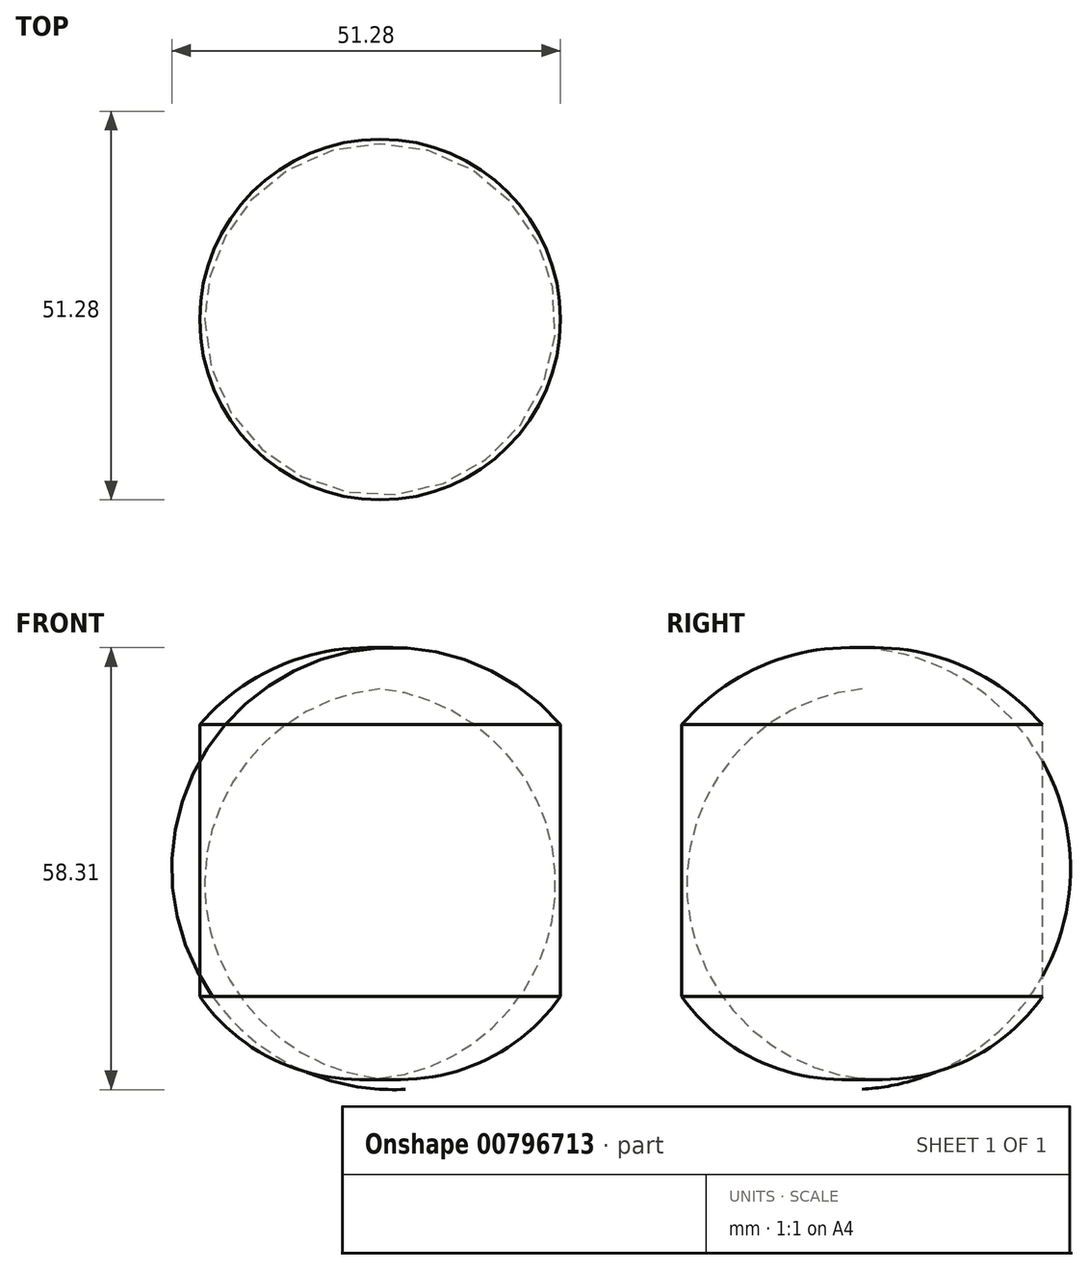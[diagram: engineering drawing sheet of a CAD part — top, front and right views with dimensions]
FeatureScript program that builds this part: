
annotation { "Feature Type Name" : "Feature", "Feature Type Description" : "" }
export const myFeature = defineFeature(function(context is Context, id is Id, definition is map)
    precondition{}
    {
        {
            var Q0;
            Q0=qCreatedBy(makeId("Front.planeOp"),FACE);
            var sketch = newSketch(context, id + "F0", { "sketchPlane" : qUnion([Q0])});
            skLineSegment(sketch, "E0.bottom", {"start": v(0, 0) * mm, "end": v(23.8, 0) * mm});
            skLineSegment(sketch, "E0.top", {"start": v(0, 35.87) * mm, "end": v(23.8, 35.87) * mm});
            skLineSegment(sketch, "E0.left", {"start": v(0, 0) * mm, "end": v(0, 35.87) * mm});
            skLineSegment(sketch, "E0.right", {"start": v(23.8, 0) * mm, "end": v(23.8, 35.87) * mm});
            skArc(sketch, "E1", {"start": v(23.8, 35.87) * mm, "mid": v(13.08, 43.7) * mm, "end": v(0, 45.99) * mm});
            skArc(sketch, "E2", {"start": v(0, -10.8) * mm, "mid": v(13.37, -8.63) * mm, "end": v(23.8, 0) * mm});
            skLineSegment(sketch, "E3", {"start": v(0, 45.99) * mm, "end": v(0, -10.8) * mm});
            skSolve(sketch);
        }
        {
            var Q0;
            {var subQ0=sQuery(id+"F0.wireOp",EDGE,"E0.bottom");Q0=makeQuery(id+"F0.imprint","IMPRINT",FACE,{"disambiguationData":[TD([[makeQuery(id+"F0.imprint","IMPRINT",EDGE,{"derivedFrom":subQ0}),-1.0]])]});}
            var Q1;
            {var subQ0=sQuery(id+"F0.wireOp",EDGE,"E0.bottom");Q1=makeQuery(id+"F0.imprint","IMPRINT",FACE,{"disambiguationData":[TD([[makeQuery(id+"F0.imprint","IMPRINT",EDGE,{"derivedFrom":subQ0}),1.0]])]});}
            var Q2;
            {var subQ0=sQuery(id+"F0.wireOp",EDGE,"E0.top");Q2=makeQuery(id+"F0.imprint","IMPRINT",FACE,{"disambiguationData":[TD([[makeQuery(id+"F0.imprint","IMPRINT",EDGE,{"derivedFrom":subQ0}),1.0]])]});}
            var Q3;
            Q3=sQuery(id+"F0.wireOp",EDGE,"E3");
            revolve(context, id + "F1", {"surfaceOperationType" : NewSurfaceOperationType.NEW, "entities" : qUnion([Q0, Q1, Q2]), "axis" : qUnion([Q3]), "revolveType" : RevolveType.FULL});
        }
    });
